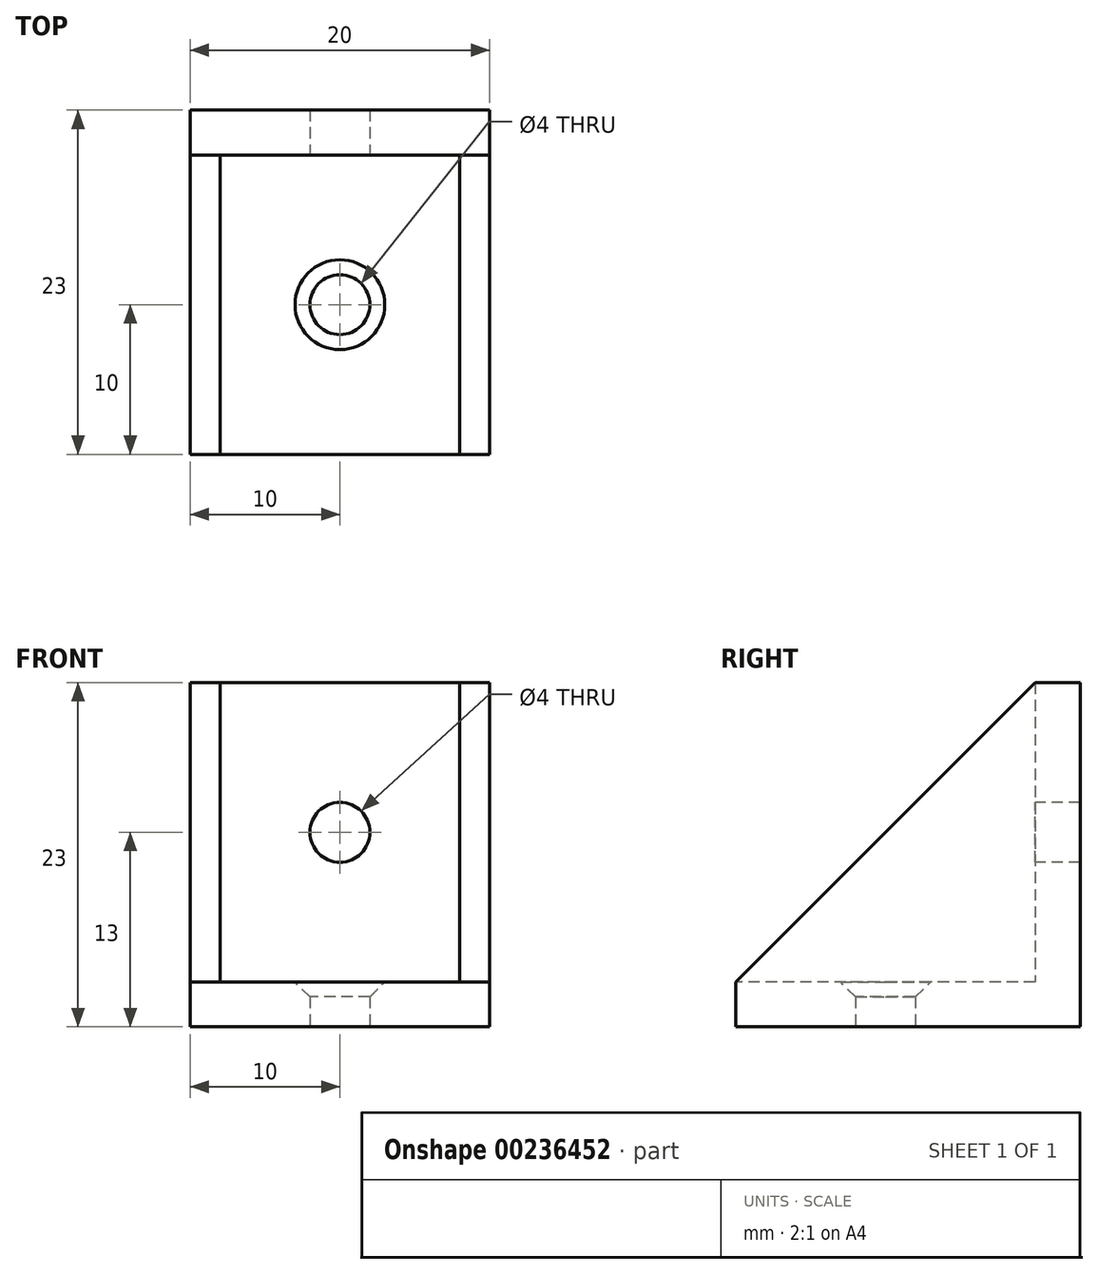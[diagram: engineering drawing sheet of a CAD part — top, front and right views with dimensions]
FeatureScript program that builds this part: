
annotation { "Feature Type Name" : "Feature", "Feature Type Description" : "" }
export const myFeature = defineFeature(function(context is Context, id is Id, definition is map)
    precondition{}
    {
        {
            var Q0;
            Q0=qCreatedBy(makeId("Top.planeOp"),FACE);
            var sketch = newSketch(context, id + "F0", { "sketchPlane" : qUnion([Q0])});
            skLineSegment(sketch, "E0.bottom", {"start": v(0, 0) * mm, "end": v(20, 0) * mm});
            skLineSegment(sketch, "E0.top", {"start": v(0, -23) * mm, "end": v(20, -23) * mm});
            skLineSegment(sketch, "E0.left", {"start": v(0, 0) * mm, "end": v(0, -23) * mm});
            skLineSegment(sketch, "E0.right", {"start": v(20, 0) * mm, "end": v(20, -23) * mm});
            skLineSegment(sketch, "E1", {"start": v(10, 0) * mm, "end": v(10, -23) * mm, "construction": true});
            skLineSegment(sketch, "E2", {"start": v(0, -13) * mm, "end": v(20, -13) * mm, "construction": true});
            skCircle(sketch, "E3", {"center": v(10, -13) * mm, "radius": 2 * mm});
            skSolve(sketch);
        }
        {
            var Q0;
            Q0=makeQuery(id+"F0.imprint","IMPRINT",FACE,{"disambiguationData":[TD([[makeQuery(id+"F0.imprint","IMPRINT",EDGE,{"derivedFrom":sQuery(id+"F0.wireOp",EDGE,"E0.bottom")}),-1.0]])]});
            extrude(context, id + "F1", {"entities" : qUnion([Q0]), "depth" : 3 * mm});
        }
        {
            var Q0;
            Q0=makeQuery(id+"F1.opExtrude","CAP_FACE",FACE,{"disambiguationData":[OSD([sQuery(id+"F0.wireOp",EDGE,"E0.bottom"),sQuery(id+"F0.wireOp",EDGE,"E0.top"),sQuery(id+"F0.wireOp",EDGE,"E0.left"),sQuery(id+"F0.wireOp",EDGE,"E0.right"),sQuery(id+"F0.wireOp",EDGE,"E3")])],"isStart":false});
            var sketch = newSketch(context, id + "F2", { "sketchPlane" : qUnion([Q0])});
            skLineSegment(sketch, "E4.bottom", {"start": v(0, 0) * mm, "end": v(20, 0) * mm});
            skLineSegment(sketch, "E4.top", {"start": v(0, -3) * mm, "end": v(20, -3) * mm});
            skLineSegment(sketch, "E4.left", {"start": v(0, 0) * mm, "end": v(0, -3) * mm});
            skLineSegment(sketch, "E4.right", {"start": v(20, 0) * mm, "end": v(20, -3) * mm});
            skSolve(sketch);
        }
        {
            var Q0;
            Q0=makeQuery(id+"F2.imprint","IMPRINT",FACE,{"disambiguationData":[TD([[makeQuery(id+"F2.imprint","IMPRINT",EDGE,{"derivedFrom":sQuery(id+"F2.wireOp",EDGE,"E4.bottom")}),-1.0]])]});
            extrude(context, id + "F3", {"entities" : qUnion([Q0]), "operationType" : NewBodyOperationType.ADD, "depth" : 20 * mm});
        }
        {
            var Q0;
            Q0=makeQuery(id+"F3.opExtrude","SWEPT_FACE",FACE,{"disambiguationData":[OSD([sQuery(id+"F2.wireOp",EDGE,"E4.top")])]});
            var sketch = newSketch(context, id + "F4", { "sketchPlane" : qUnion([Q0])});
            skLineSegment(sketch, "E5", {"start": v(0, 13) * mm, "end": v(20, 13) * mm, "construction": true});
            skLineSegment(sketch, "E6", {"start": v(10, 23) * mm, "end": v(10, 3) * mm, "construction": true});
            skCircle(sketch, "E7", {"center": v(10, 13) * mm, "radius": 2 * mm});
            skSolve(sketch);
        }
        {
            var Q0;
            Q0=makeQuery(id+"F4.imprint","IMPRINT",FACE,{"disambiguationData":[TD([[makeQuery(id+"F4.imprint","IMPRINT",EDGE,{"derivedFrom":sQuery(id+"F4.wireOp",EDGE,"E7")}),1.0]])]});
            extrude(context, id + "F5", {"entities" : qUnion([Q0]), "operationType" : NewBodyOperationType.REMOVE, "endBound" : BoundingType.THROUGH_ALL, "oppositeDirection" : true, "depth" : 25 * mm});
        }
        {
            var Q0;
            Q0=makeQuery(id+"F3.boolean.opBoolean","MERGE",FACE,{"derivedFrom":[makeQuery(id+"F1.opExtrude","SWEPT_FACE",FACE,{"disambiguationData":[OSD([sQuery(id+"F0.wireOp",EDGE,"E0.right")])]}),makeQuery(id+"F3.opExtrude","SWEPT_FACE",FACE,{"disambiguationData":[OSD([sQuery(id+"F2.wireOp",EDGE,"E4.right")])]})]});
            var sketch = newSketch(context, id + "F6", { "sketchPlane" : qUnion([Q0])});
            skLineSegment(sketch, "E8.0", {"start": v(-3, 23) * mm, "end": v(-3, 3) * mm});
            skLineSegment(sketch, "E9.0", {"start": v(-3, 3) * mm, "end": v(-23, 3) * mm});
            skLineSegment(sketch, "E10", {"start": v(-23, 3) * mm, "end": v(-3, 23) * mm});
            skSolve(sketch);
        }
        {
            var Q0;
            Q0=makeQuery(id+"F6.imprint","IMPRINT",FACE,{"disambiguationData":[TD([[makeQuery(id+"F6.imprint","IMPRINT",EDGE,{"derivedFrom":sQuery(id+"F6.wireOp",EDGE,"E8.0")}),-1.0]])]});
            extrude(context, id + "F7", {"entities" : qUnion([Q0]), "operationType" : NewBodyOperationType.ADD, "oppositeDirection" : true, "depth" : 2 * mm});
        }
        {
            var Q0;
            Q0=makeQuery(id+"F3.boolean.opBoolean","MERGE",FACE,{"derivedFrom":[makeQuery(id+"F1.opExtrude","SWEPT_FACE",FACE,{"disambiguationData":[OSD([sQuery(id+"F0.wireOp",EDGE,"E0.left")])]}),makeQuery(id+"F3.opExtrude","SWEPT_FACE",FACE,{"disambiguationData":[OSD([sQuery(id+"F2.wireOp",EDGE,"E4.left")])]})]});
            var sketch = newSketch(context, id + "F8", { "sketchPlane" : qUnion([Q0])});
            skLineSegment(sketch, "E11.0", {"start": v(3, 23) * mm, "end": v(3, 3) * mm});
            skLineSegment(sketch, "E12.0", {"start": v(3, 3) * mm, "end": v(23, 3) * mm});
            skLineSegment(sketch, "E13", {"start": v(3, 23) * mm, "end": v(23, 3) * mm});
            skSolve(sketch);
        }
        {
            var Q0;
            Q0=makeQuery(id+"F8.imprint","IMPRINT",FACE,{"disambiguationData":[TD([[makeQuery(id+"F8.imprint","IMPRINT",EDGE,{"derivedFrom":sQuery(id+"F8.wireOp",EDGE,"E11.0")}),1.0]])]});
            extrude(context, id + "F9", {"entities" : qUnion([Q0]), "operationType" : NewBodyOperationType.ADD, "oppositeDirection" : true, "depth" : 2 * mm});
        }
        {
            var Q0;
            Q0=makeQuery(id+"F1.opExtrude","CAP_EDGE",EDGE,{"disambiguationData":[OSD([sQuery(id+"F0.wireOp",EDGE,"E3")])],"isStart":false});
            var Q1;
            Q1=makeQuery(id+"F5.boolean.opBoolean","COPY",EDGE,{"derivedFrom":makeQuery(id+"F5.opExtrude","CAP_EDGE",EDGE,{"disambiguationData":[OSD([sQuery(id+"F4.wireOp",EDGE,"E7")])],"isStart":true})});
            chamfer(context, id + "F10", {"entities" : qUnion([Q0, Q1]), "width" : 1 * mm, "tangentPropagation" : true});
        }
    });
